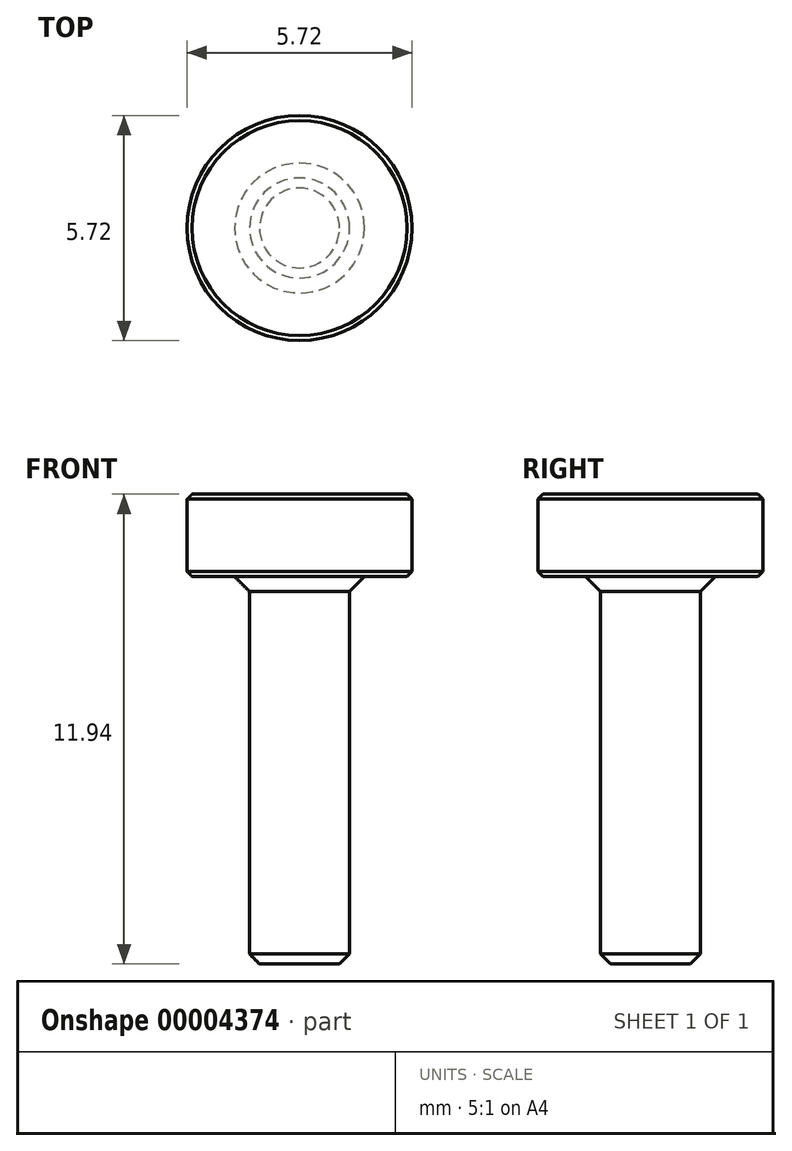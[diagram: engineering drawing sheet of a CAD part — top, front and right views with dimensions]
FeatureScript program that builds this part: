
annotation { "Feature Type Name" : "Feature", "Feature Type Description" : "" }
export const myFeature = defineFeature(function(context is Context, id is Id, definition is map)
    precondition{}
    {
        {
            var Q0;
            Q0=qCreatedBy(makeId("Front.planeOp"),FACE);
            var sketch = newSketch(context, id + "F0", { "sketchPlane" : qUnion([Q0])});
            skLineSegment(sketch, "E0.bottom", {"start": v(0, 0) * mm, "end": v(-1.27, 0) * mm});
            skLineSegment(sketch, "E0.left", {"start": v(0, 0) * mm, "end": v(0, 11.94) * mm});
            skLineSegment(sketch, "E0.right", {"start": v(-1.27, 0) * mm, "end": v(-1.27, 9.84) * mm});
            skLineSegment(sketch, "E1.bottom", {"start": v(-1.27, 9.84) * mm, "end": v(-2.86, 9.84) * mm});
            skLineSegment(sketch, "E1.top", {"start": v(0, 11.94) * mm, "end": v(-2.86, 11.94) * mm});
            skLineSegment(sketch, "E1.right", {"start": v(-2.86, 9.84) * mm, "end": v(-2.86, 11.94) * mm});
            skSolve(sketch);
        }
        {
            var Q0;
            Q0=makeQuery(id+"F0.imprint","IMPRINT",FACE,{"disambiguationData":[TD([[makeQuery(id+"F0.imprint","IMPRINT",EDGE,{"derivedFrom":sQuery(id+"F0.wireOp",EDGE,"E0.bottom")}),-1.0]])]});
            var Q1;
            Q1=sQuery(id+"F0.wireOp",EDGE,"E0.left");
            revolve(context, id + "F1", {"surfaceOperationType" : NewSurfaceOperationType.NEW, "entities" : qUnion([Q0]), "axis" : qUnion([Q1]), "revolveType" : RevolveType.FULL});
        }
        {
            var Q0;
            Q0=makeQuery(id+"F1.opRevolve","SWEPT_EDGE",EDGE,{"disambiguationData":[OSD([sQuery(id+"F0.wireOp",EDGE,"E0.bottom"),sQuery(id+"F0.wireOp",EDGE,"E0.right")])]});
            chamfer(context, id + "F2", {"entities" : qUnion([Q0]), "width" : 0.25 * mm, "tangentPropagation" : true});
        }
        {
            var Q0;
            Q0=makeQuery(id+"F1.opRevolve","SWEPT_EDGE",EDGE,{"disambiguationData":[OSD([sQuery(id+"F0.wireOp",EDGE,"E0.right"),sQuery(id+"F0.wireOp",EDGE,"E1.bottom")])]});
            chamfer(context, id + "F3", {"entities" : qUnion([Q0]), "width" : 0.38 * mm, "tangentPropagation" : true});
        }
        {
            var Q0;
            Q0=makeQuery(id+"F1.opRevolve","SWEPT_EDGE",EDGE,{"disambiguationData":[OSD([sQuery(id+"F0.wireOp",EDGE,"E1.bottom"),sQuery(id+"F0.wireOp",EDGE,"E1.right")])]});
            var Q1;
            Q1=makeQuery(id+"F1.opRevolve","SWEPT_EDGE",EDGE,{"disambiguationData":[OSD([sQuery(id+"F0.wireOp",EDGE,"E1.top"),sQuery(id+"F0.wireOp",EDGE,"E1.right")])]});
            chamfer(context, id + "F4", {"entities" : qUnion([Q0, Q1]), "width" : 0.13 * mm, "tangentPropagation" : true});
        }
    });
